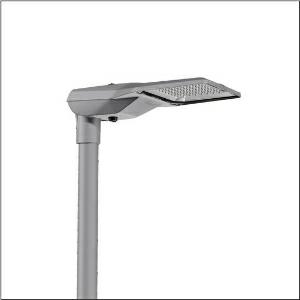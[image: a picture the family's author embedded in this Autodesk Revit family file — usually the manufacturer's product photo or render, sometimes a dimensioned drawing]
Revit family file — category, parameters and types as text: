
# Revit family: streetlight_sl_21_midi___p0_8a_5xe3u33t08mb_d2fa
name_source: partatom
category: Lighting Fixtures
units: mm (PartAtom-declared; Revit-internal decimal feet)

## family parameters
Cut with Voids When Loaded = No
Host = Face
Light Source = No
Part Type = Normal
Room Calculation Point = No
Round Connector Dimension = Use Diameter
Shared = No

## types (1)
- --- (1 x LED, 18430 lm, 136 W, 3000K)
    Apparent Load = 136 VA
    CIE Flux Codes = 33 69 96 100 100
    Color Rendering = 70
    Color Temperature = 3000K
    Default Elevation = 1800 mm
    Description = Streetlight SL 21 midi, mast luminaire, primary light control with lens, of PMMA, primary optical cover: cover, of toughened safety glass, transparent, light distribution: P0.8a, light emission: direct distribution, primary light characteristic: asymmetric, installation type: post-top, side-entry, LED, High Power LED, rated luminous flux: 18.430lm, luminous efficacy: 136lm/W, light colour: 730, colour temperature: 3000K, control gear: D4i, control: pre-setting: logarithmic dimming characteristic, flexible luminous flux parameterisation, time-dependent luminous flux control, constant luminous flux control, overheat protection, mains connection: 230..240V, AC, 50/60Hz, start of lifetime: 136W, end of service life: 142W, reduction: 61W, luminaire housing, of diecast aluminium, powder-coated, SITECO metallic grey (DB 702S), corrosivity category C5 high according to DIN EN ISO 12944, multi-level sealing system, sealing non-destructively replaceable, inclination adjustable: 0°, 5°, 10°, 15°, please order mast flange separately, length: 644mm, width: 335mm, height: 110mm, mast flange for spigot size: 42mm (side-entry): 5XC10008XM4, 60/48mm (side-entry/post-top): 5XC10108XM2, 76/60mm (side-entry/post-top): 5XC10108XM1, mounting height: 4..8m, Smart Interface below and above, protection rating (complete): IP66, insulation class (complete): insulation class II (safety insulation), certification: CE, ENEC, ENEC+, VDE, impact resistance: IK10, permissible operating ambient temperature for outdoor applications: -40..+50°C, standard-compliant lighting for roads and squares, packaging unit: 1 piece

Light Distribution: P0.8a
    Height = 111 mm
    Lamp = 1 x LED
    Lamp Light Flux = 18430 lm
    Lamp Power = 136 W
    Lamp count = 1
    Length = 644 mm
    Luminous efficacy = 136 lm/W
    Manufacturer = Siteco
    ModVariant = No
    Model = 5XE3U33T08MB
    Number of Poles = 1
    OnlyDefault = Yes
    Power Factor = 1
    Product Name = Streetlight SL 21 midi | P0.8a
    Product group = mast luminaire | pylon top
    ProductGroupID = 6100
    Protection Class = Protection class II
    Protection Degree = IP 66
    RLX_Detail_Level = 1
    RLX_Emergency_Light_Flux = 0 lm
    RLX_Emergency_Type = 0
    RLX_Emergency_Type_DB = No
    RlxData = <blob elided: 90341 chars, md5=48531c1f>
    Socket = socket
    Standby Power = 0 W
    System Light Flux = 18429 lm
    System Power = 136 W
    Type Comments = factory setting: luminous flux: 100 % | dim-lin: 254 | 695 mA
    Type Image = l_1004304.jpg
    URL = http://relux.com
    VarID = @adj_080327
    Voltage = 0 V
    Weight = 0.00 kg
    Width = 336 mm

## geometry (parser evidence)
native form markers: Blend x4, Sweep x10
no freeform markers — native parametric forms only
